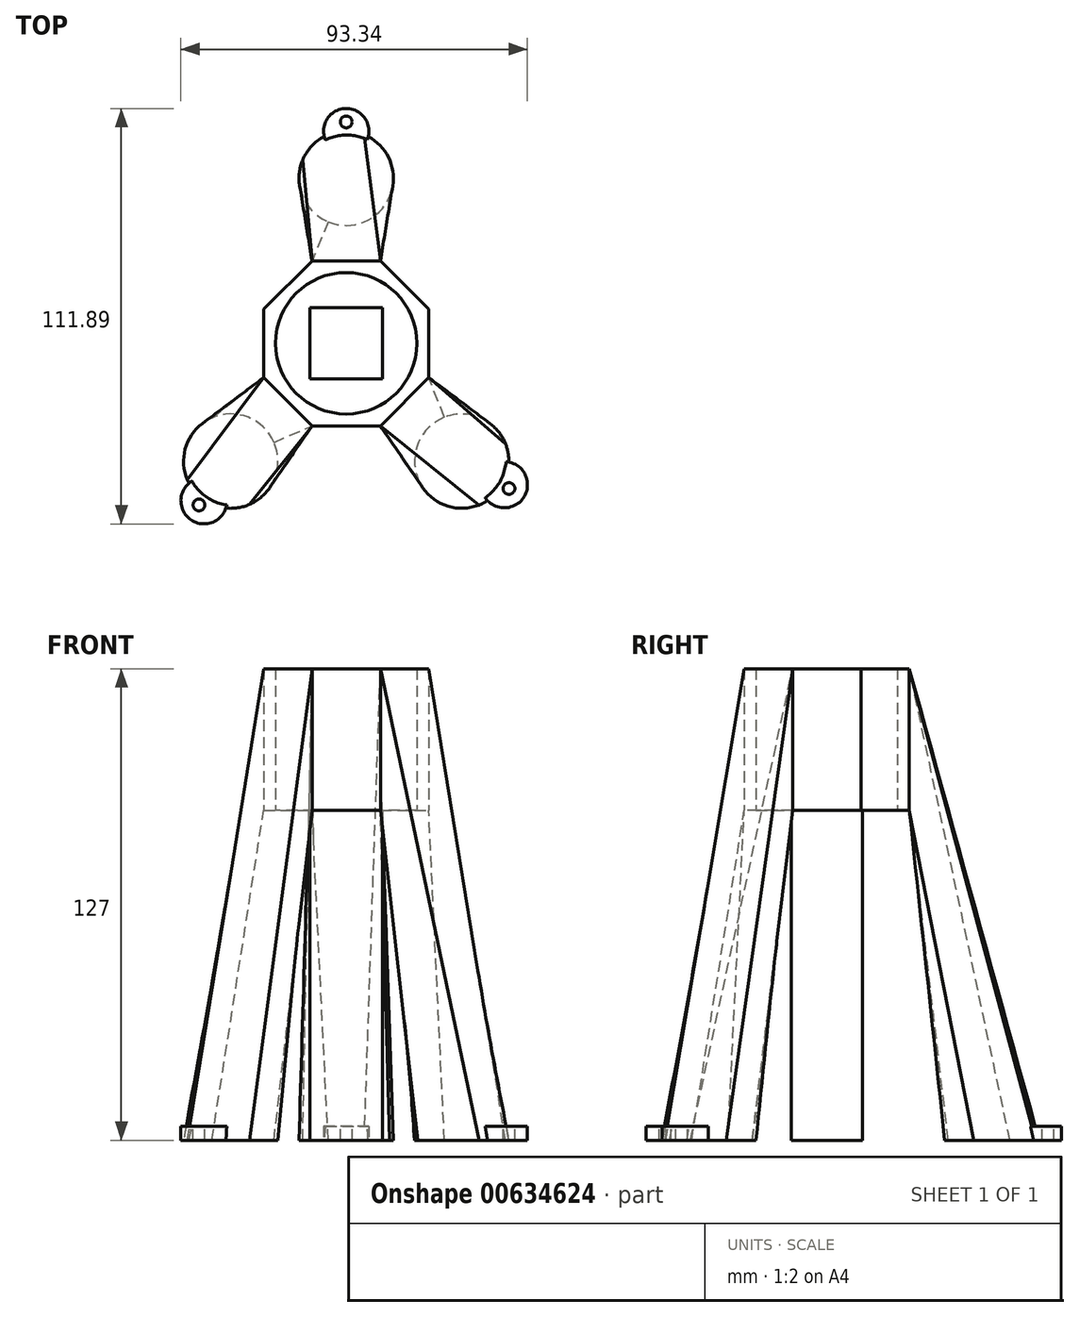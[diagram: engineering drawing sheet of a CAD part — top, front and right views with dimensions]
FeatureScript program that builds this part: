
annotation { "Feature Type Name" : "Feature", "Feature Type Description" : "" }
export const myFeature = defineFeature(function(context is Context, id is Id, definition is map)
    precondition{}
    {
        {
            var Q0;
            Q0=qCreatedBy(makeId("Top.planeOp"),FACE);
            var sketch = newSketch(context, id + "F0", { "sketchPlane" : qUnion([Q0])});
            skLineSegment(sketch, "E0.bottom", {"start": v(9.76, -9.62) * mm, "end": v(-9.76, -9.62) * mm});
            skLineSegment(sketch, "E0.top", {"start": v(9.76, 9.62) * mm, "end": v(-9.76, 9.62) * mm});
            skLineSegment(sketch, "E0.left", {"start": v(9.76, -9.62) * mm, "end": v(9.76, 9.62) * mm});
            skLineSegment(sketch, "E0.right", {"start": v(-9.76, -9.62) * mm, "end": v(-9.76, 9.62) * mm});
            skPoint(sketch, "E0.middle", {"position": v(0, 0) * mm});
            skSolve(sketch);
        }
        {
            var Q0;
            Q0 = qSketchRegion(id + "F0", true);
            extrude(context, id + "F1", {"entities" : qUnion([Q0]), "depth" : 88.9 * mm, "offsetDistance" : 25.4 * mm});
        }
        {
            var Q0;
            Q0=makeQuery(id+"F1.opExtrude","CAP_FACE",FACE,{"disambiguationData":[OSD([sQuery(id+"F0.wireOp",EDGE,"E0.bottom"),sQuery(id+"F0.wireOp",EDGE,"E0.top"),sQuery(id+"F0.wireOp",EDGE,"E0.left"),sQuery(id+"F0.wireOp",EDGE,"E0.right")])],"isStart":false});
            var sketch = newSketch(context, id + "F2", { "sketchPlane" : qUnion([Q0])});
            skCircle(sketch, "E1", {"center": v(0, 0) * mm, "radius": 19.05 * mm});
            skCircle(sketch, "E2", {"center": v(0, 0) * mm, "radius": 22.23 * mm});
            skCircle(sketch, "E3.cCircle", {"center": v(0, 0) * mm, "radius": 22.23 * mm, "construction": true});
            skLineSegment(sketch, "E3.0", {"start": v(22.23, 9.2) * mm, "end": v(22.23, -9.2) * mm});
            skLineSegment(sketch, "E3.1", {"start": v(22.23, -9.2) * mm, "end": v(9.2, -22.23) * mm});
            skLineSegment(sketch, "E3.2", {"start": v(9.2, -22.23) * mm, "end": v(-9.2, -22.23) * mm});
            skLineSegment(sketch, "E3.3", {"start": v(-9.2, -22.22) * mm, "end": v(-22.22, -9.2) * mm});
            skLineSegment(sketch, "E3.4", {"start": v(-22.23, -9.2) * mm, "end": v(-22.23, 9.2) * mm});
            skLineSegment(sketch, "E3.5", {"start": v(-22.23, 9.2) * mm, "end": v(-9.2, 22.22) * mm});
            skLineSegment(sketch, "E3.6", {"start": v(-9.2, 22.22) * mm, "end": v(9.2, 22.23) * mm});
            skLineSegment(sketch, "E3.7", {"start": v(9.2, 22.23) * mm, "end": v(22.23, 9.2) * mm});
            skPoint(sketch, "E3.0.midPoint", {"position": v(22.23, 0) * mm});
            skSolve(sketch);
        }
        {
            var Q0;
            Q0 = qSketchRegion(id + "F2", true);
            extrude(context, id + "F3", {"entities" : qUnion([Q0]), "depth" : 38.1 * mm, "offsetDistance" : 25.4 * mm});
        }
        {
            var Q0;
            Q0=qCreatedBy(makeId("Top.planeOp"),FACE);
            var sketch = newSketch(context, id + "F4", { "sketchPlane" : qUnion([Q0])});
            skCircle(sketch, "E4", {"center": v(0, 44.45) * mm, "radius": 12.7 * mm});
            skSolve(sketch);
        }
        {
            var Q1;
            Q1=makeQuery(id+"F4.imprint","IMPRINT",FACE,{"disambiguationData":[TD([[makeQuery(id+"F4.imprint","IMPRINT",EDGE,{"derivedFrom":sQuery(id+"F4.wireOp",EDGE,"E4")}),1.0]])]});
            var Q2;
            Q2=makeQuery(id+"F3.opExtrude","SWEPT_FACE",FACE,{"disambiguationData":[OSD([sQuery(id+"F2.wireOp",EDGE,"E3.6")])]});
            loft(context, id + "F5", {"operationType" : NewBodyOperationType.ADD, "sheetProfilesArray" : [{ "sheetProfileEntities" : qUnion([Q1]) }, { "sheetProfileEntities" : qUnion([Q2]) }]});
        }
        {
            var Q0;
            Q0=qCreatedBy(makeId("Top.planeOp"),FACE);
            var sketch = newSketch(context, id + "F6", { "sketchPlane" : qUnion([Q0])});
            skCircle(sketch, "E5", {"center": v(-31.1, -31.75) * mm, "radius": 12.7 * mm});
            skSolve(sketch);
        }
        {
            var Q0;
            Q0=qCreatedBy(makeId("Top.planeOp"),FACE);
            var sketch = newSketch(context, id + "F7", { "sketchPlane" : qUnion([Q0])});
            skCircle(sketch, "E6", {"center": v(31.1, -31.75) * mm, "radius": 12.7 * mm});
            skSolve(sketch);
        }
        {
            var Q1;
            Q1 = qSketchRegion(id + "F6", true);
            var Q2;
            Q2=makeQuery(id+"F3.opExtrude","SWEPT_FACE",FACE,{"disambiguationData":[OSD([sQuery(id+"F2.wireOp",EDGE,"E3.3")])]});
            loft(context, id + "F8", {"operationType" : NewBodyOperationType.ADD, "sheetProfilesArray" : [{ "sheetProfileEntities" : qUnion([Q1]) }, { "sheetProfileEntities" : qUnion([Q2]) }]});
        }
        {
            var Q1;
            Q1=makeQuery(id+"F7.imprint","IMPRINT",FACE,{"disambiguationData":[TD([[makeQuery(id+"F7.imprint","IMPRINT",EDGE,{"derivedFrom":sQuery(id+"F7.wireOp",EDGE,"E6")}),1.0]])]});
            var Q2;
            Q2=makeQuery(id+"F3.opExtrude","SWEPT_FACE",FACE,{"disambiguationData":[OSD([sQuery(id+"F2.wireOp",EDGE,"E3.1")])]});
            loft(context, id + "F9", {"operationType" : NewBodyOperationType.ADD, "sheetProfilesArray" : [{ "sheetProfileEntities" : qUnion([Q1]) }, { "sheetProfileEntities" : qUnion([Q2]) }]});
        }
        {
            var Q0;
            Q0=qCreatedBy(makeId("Top.planeOp"),FACE);
            var sketch = newSketch(context, id + "F10", { "sketchPlane" : qUnion([Q0])});
            skCircle(sketch, "E7", {"center": v(-38.3, -42.42) * mm, "radius": 6.22 * mm});
            skCircle(sketch, "E8", {"center": v(42.6, -38.1) * mm, "radius": 6.22 * mm});
            skCircle(sketch, "E9", {"center": v(0, 57.15) * mm, "radius": 6.1 * mm});
            skSolve(sketch);
        }
        {
            var Q0;
            Q0 = qSketchRegion(id + "F10", true);
            extrude(context, id + "F11", {"entities" : qUnion([Q0]), "operationType" : NewBodyOperationType.ADD, "depth" : 3.8 * mm, "offsetDistance" : 25.4 * mm});
        }
        {
            var Q0;
            Q0=makeQuery(id+"F11.opExtrude","CAP_FACE",FACE,{"disambiguationData":[OSD([sQuery(id+"F10.wireOp",EDGE,"E7")])],"isStart":false});
            var sketch = newSketch(context, id + "F12", { "sketchPlane" : qUnion([Q0])});
            skPoint(sketch, "E10", {"position": v(43.85, -39.12) * mm});
            skPoint(sketch, "E11", {"position": v(0, 59.61) * mm});
            skPoint(sketch, "E12", {"position": v(-39.66, -43.54) * mm});
            skSolve(sketch);
        }
        {
            var Q0;
            Q0=sQuery(id+"F12.wireOp",VERTEX,"E10");
            var Q1;
            Q1=sQuery(id+"F12.wireOp",VERTEX,"E11");
            var Q2;
            Q2=sQuery(id+"F12.wireOp",VERTEX,"E12");
            var Q3;
            Q3=makeQuery(id+"F3.opExtrude","SWEPT_BODY",BODY,{"disambiguationData":[OSD([sQuery(id+"F2.wireOp",EDGE,"E1"),sQuery(id+"F2.wireOp",EDGE,"E3.0"),sQuery(id+"F2.wireOp",EDGE,"E3.1"),sQuery(id+"F2.wireOp",EDGE,"E3.2"),sQuery(id+"F2.wireOp",EDGE,"E3.3"),sQuery(id+"F2.wireOp",EDGE,"E3.4"),sQuery(id+"F2.wireOp",EDGE,"E3.5"),sQuery(id+"F2.wireOp",EDGE,"E3.6"),sQuery(id+"F2.wireOp",EDGE,"E3.7")])]});
            hole(context, id + "F13", {"style" : HoleStyle.SIMPLE, "endStyle" : HoleEndStyle.THROUGH, "holeDiameter" : 3.17 * mm, "majorDiameter" : 6.35 * mm, "isTappedThrough" : true, "tappedDepth" : 12.7 * mm, "tapClearance" : 3, "startFromSketch" : true, "locations" : qUnion([Q0, Q1, Q2]), "scope" : qUnion([Q3])});
        }
    });
